# Revit family: QF_MACOM_PRx-xx
name_source: partatom
category: Equipamento especial
units: mm (PartAtom-declared; Revit-internal decimal feet)

## family parameters
Com base no plano de trabalho = Não
Compartilhado = Não
Corte com vazios quando carregada = Não
Cota do conector redondo = Utilizar diâmetro
Número OmniClass = 23.40.40.11.11.11
Ponto de cálculo do ambiente = Não
Sempre na vertical = Sim
Tipo de parte = Normal
Título OmniClass = Refrigerators

## types (20) — shared parameters
Climate Class = 4
Coolant = R134a
Cycle = 60 Hz
Descrição = PISTA REFRIGERADA MACOM
Elevação padrão = 0,000 mm
Fabricante = MACOM
Max Room Temperature = 30,000 °C
Protection Degree = IP 22
Show Logo = Sim
URL = https://www.acosmacom.com.br
Volts = 220 V
Weight = 0,00 lbm
Width = 590,000 mm
Work Temperature = 0°C a 2°C

## per-type parameters (varying)
| type | Electric Power | GN Capacity 1/1 | Height | Length | PL Plate | Volume |
| PR2-160 | 360 W | 02 | 544,000 mm | 715,000 mm | Não | 0,23 m³ |
| PR2-25 | 360 W | 02 | 409,000 mm | 715,000 mm | Não | 0,23 m³ |
| PR2-65 | 360 W | 02 | 449,000 mm | 715,000 mm | Não | 0,23 m³ |
| PR3-25 | 360 W | 03 | 409,000 mm | 1040,000 mm | Não | 0,34 m³ |
| PR3-65 | 360 W | 03 | 449,000 mm | 1040,000 mm | Não | 0,34 m³ |
| PR3-160 | 360 W | 03 | 544,000 mm | 1040,000 mm | Não | 0,34 m³ |
| PR4-25 | 400 W | 04 | 409,000 mm | 1343,000 mm | Não | 0,44 m³ |
| PR4-65 | 400 W | 04 | 449,000 mm | 1343,000 mm | Não | 0,44 m³ |
| PR4-160 | 400 W | 04 | 544,000 mm | 1343,000 mm | Não | 0,44 m³ |
| PR5-25 | 400 W | 05 | 409,000 mm | 1690,000 mm | Não | 0,55 m³ |
| PR5-65 | 400 W | 05 | 449,000 mm | 1690,000 mm | Não | 0,55 m³ |
| PR5-160 | 400 W | 05 | 544,000 mm | 1690,000 mm | Não | 0,55 m³ |
| PR6-25 | 400 W | 06 | 409,000 mm | 2015,000 mm | Não | 0,55 m³ |
| PR6-65 | 400 W | 06 | 449,000 mm | 2015,000 mm | Não | 0,55 m³ |
| PR6-160 | 400 W | 06 | 544,000 mm | 2015,000 mm | Não | 0,55 m³ |
| PR6-PL | 400 W | 06 | 384,000 mm | 2015,000 mm | Sim | 0,65 m³ |
| PR5-PL | 400 W | 05 | 384,000 mm | 1690,000 mm | Sim | 0,55 m³ |
| PR4-PL | 400 W | 04 | 384,000 mm | 1365,000 mm | Sim | 0,44 m³ |
| PR3-PL | 360 W | 03 | 384,000 mm | 1040,000 mm | Sim | 0,34 m³ |
| PR2-PL | 360 W | 02 | 384,000 mm | 715,000 mm | Sim | 0,23 m³ |

note: column(s) folded — value = type name in every type: Modelo

## geometry (parser evidence)
native form markers: Sweep x6
no freeform markers — native parametric forms only
